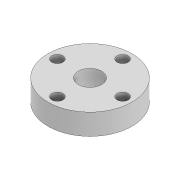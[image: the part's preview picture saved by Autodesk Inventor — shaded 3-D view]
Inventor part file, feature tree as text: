
AUTODESK INVENTOR PART (.ipt)
format: ipt  version: 2022 (Build 260153000, 153)  size: 103,424 bytes
history: native  units: mm
features: extrude x1, sketch x1
ambient origin geometry x8: Origin, YZ Plane, XZ Plane, XY Plane, X Axis, Y Axis, Z Axis, Center Point
bodies: Solid1 (feature_tree)
feature tree (2):
  extrude  "Extrusion1"  Depth=4.5mm
  sketch  "Sketch1"  dims[d0=18.0mm d1=5.0mm d2=2.4mm d3=7.0mm d4=40.0mm d6=360.0deg d8=4.5mm d9=0.0mm]
